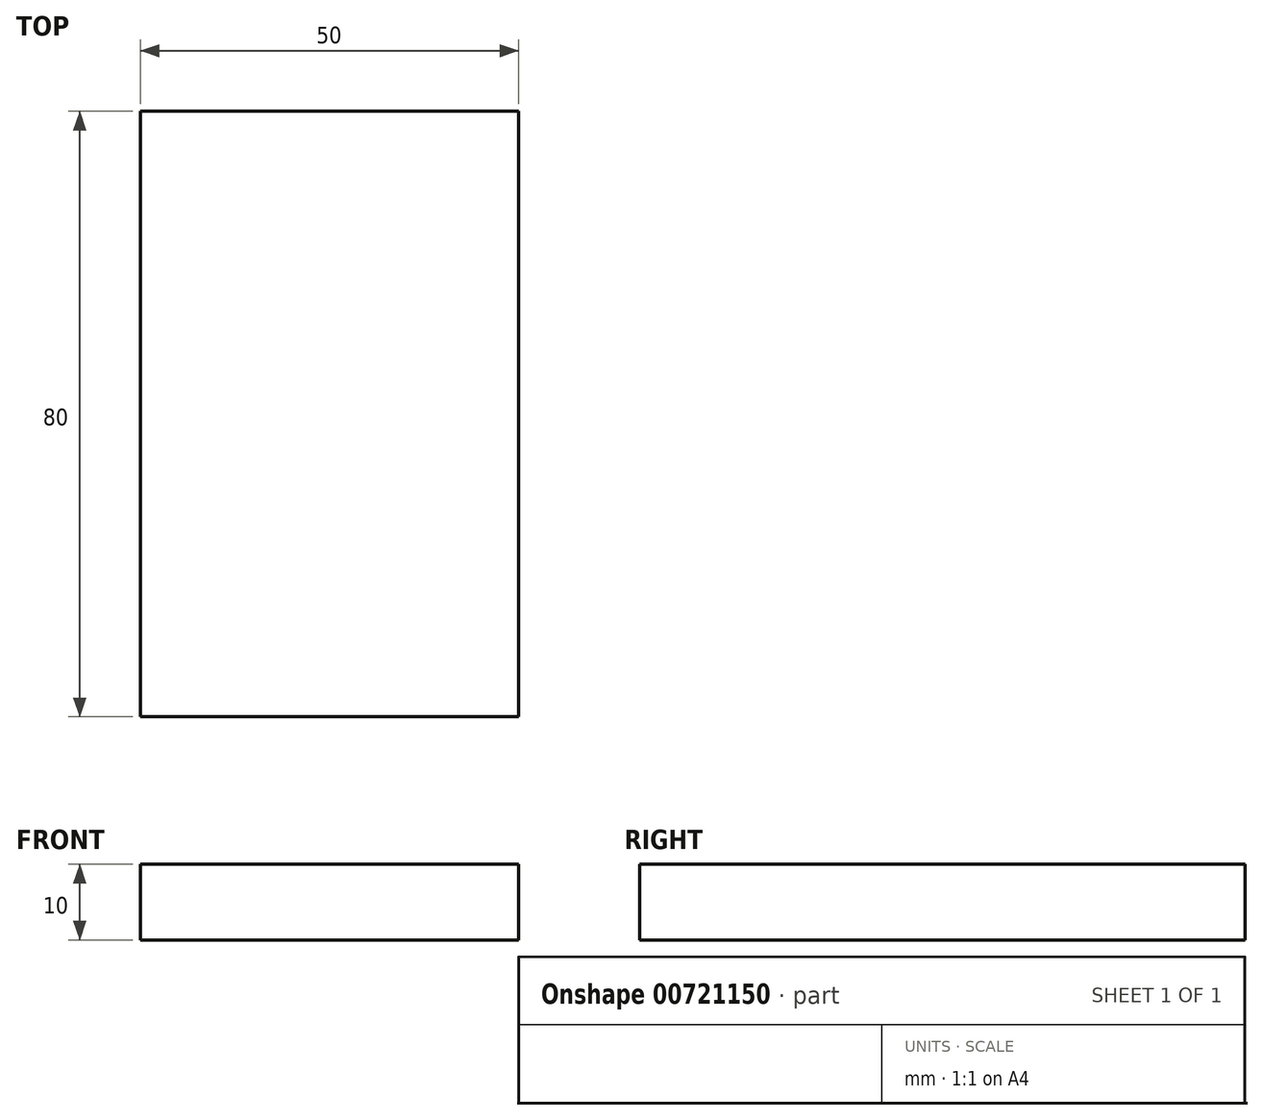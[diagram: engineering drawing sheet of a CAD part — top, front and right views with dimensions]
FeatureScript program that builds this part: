
annotation { "Feature Type Name" : "Feature", "Feature Type Description" : "" }
export const myFeature = defineFeature(function(context is Context, id is Id, definition is map)
    precondition{}
    {
        {
            var Q0;
            Q0=qCreatedBy(makeId("Front.planeOp"),FACE);
            var sketch = newSketch(context, id + "F0", { "sketchPlane" : qUnion([Q0])});
            skLineSegment(sketch, "E0.bottom", {"start": v(25, -5) * mm, "end": v(-25, -5) * mm});
            skLineSegment(sketch, "E0.top", {"start": v(25, 5) * mm, "end": v(-25, 5) * mm});
            skLineSegment(sketch, "E0.left", {"start": v(25, -5) * mm, "end": v(25, 5) * mm});
            skLineSegment(sketch, "E0.right", {"start": v(-25, -5) * mm, "end": v(-25, 5) * mm});
            skPoint(sketch, "E0.middle", {"position": v(0, 0) * mm});
            skSolve(sketch);
        }
        {
            var Q0;
            Q0=makeQuery(id+"F0.imprint","IMPRINT",FACE,{"disambiguationData":[TD([[makeQuery(id+"F0.imprint","IMPRINT",EDGE,{"derivedFrom":sQuery(id+"F0.wireOp",EDGE,"E0.bottom")}),-1.0]])]});
            extrude(context, id + "F1", {"entities" : qUnion([Q0]), "depth" : 80 * mm, "offsetDistance" : 25 * mm});
        }
    });
